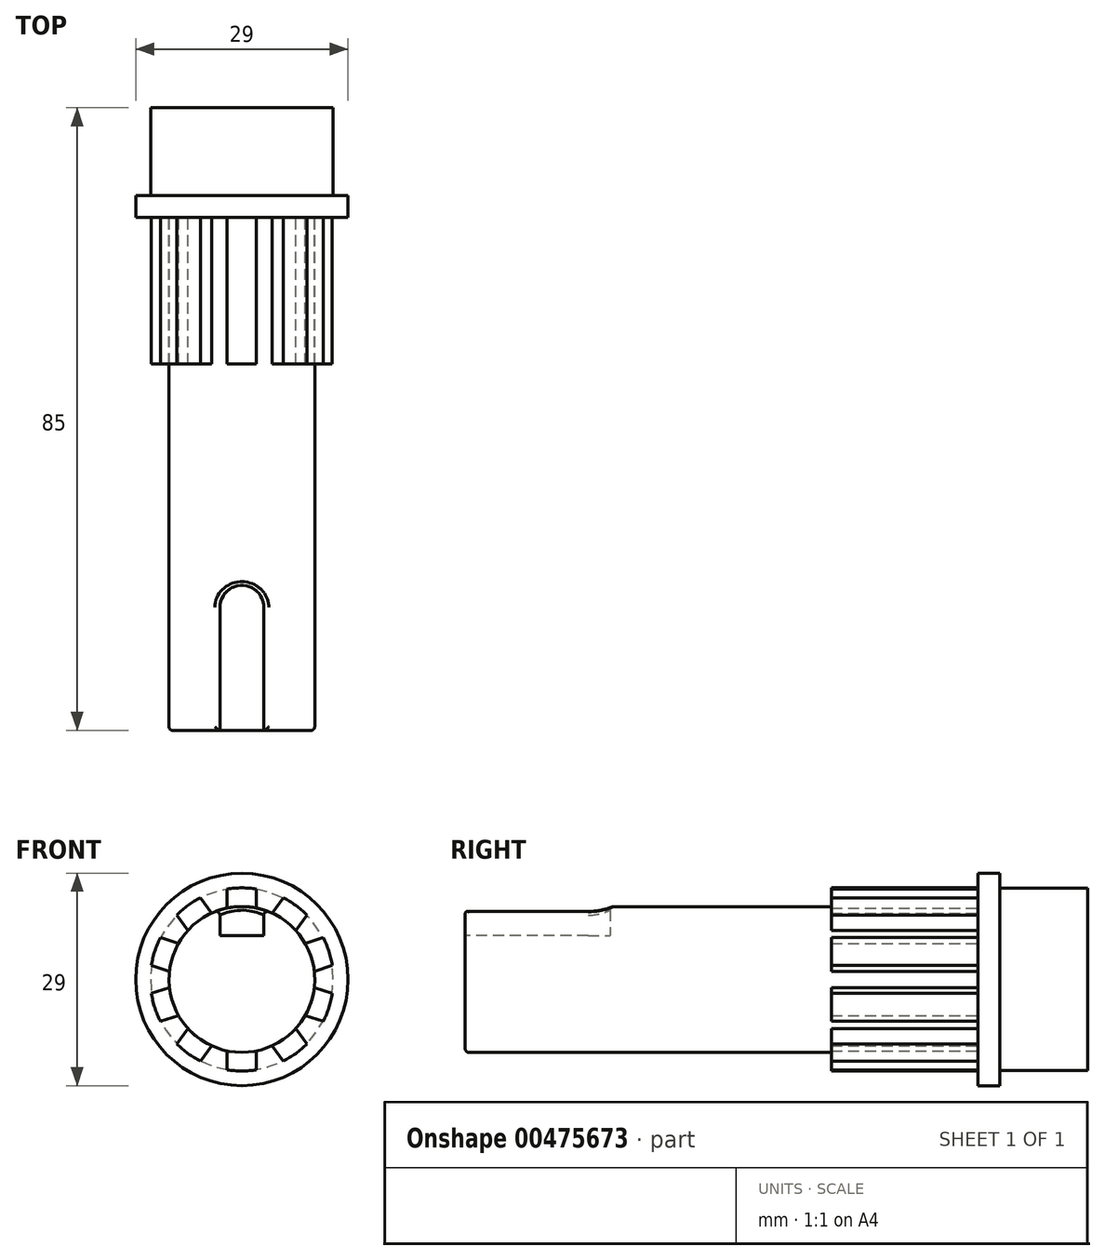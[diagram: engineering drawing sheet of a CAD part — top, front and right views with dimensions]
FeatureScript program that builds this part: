
annotation { "Feature Type Name" : "Feature", "Feature Type Description" : "" }
export const myFeature = defineFeature(function(context is Context, id is Id, definition is map)
    precondition{}
    {
        {
            var Q0;
            Q0=qCreatedBy(makeId("Front.planeOp"),FACE);
            var sketch = newSketch(context, id + "F0", { "sketchPlane" : qUnion([Q0])});
            skCircle(sketch, "E0", {"center": v(0, 0) * mm, "radius": 14.5 * mm});
            skCircle(sketch, "E1", {"center": v(0, 0) * mm, "radius": 12.45 * mm});
            skCircle(sketch, "E2", {"center": v(0, 0) * mm, "radius": 9.95 * mm});
            skSolve(sketch);
        }
        {
            var Q0;
            Q0=makeQuery(id+"F0.imprint","IMPRINT",FACE,{"disambiguationData":[TD([[makeQuery(id+"F0.imprint","IMPRINT",EDGE,{"derivedFrom":sQuery(id+"F0.wireOp",EDGE,"E2")}),1.0]])]});
            var Q1;
            Q1=sQuery(id+"F0.wireOp",EDGE,"E2");
            extrude(context, id + "F1", {"entities" : qUnion([Q0]), "surfaceEntities" : qUnion([Q1]), "depth" : 70 * mm});
        }
        {
            var Q0;
            Q0=makeQuery(id+"F0.imprint","IMPRINT",FACE,{"disambiguationData":[TD([[makeQuery(id+"F0.imprint","IMPRINT",EDGE,{"derivedFrom":sQuery(id+"F0.wireOp",EDGE,"E1")}),1.0]])]});
            var Q1;
            Q1=makeQuery(id+"F0.imprint","IMPRINT",FACE,{"disambiguationData":[TD([[makeQuery(id+"F0.imprint","IMPRINT",EDGE,{"derivedFrom":sQuery(id+"F0.wireOp",EDGE,"E2")}),1.0]])]});
            extrude(context, id + "F2", {"entities" : qUnion([Q0, Q1]), "operationType" : NewBodyOperationType.ADD, "oppositeDirection" : true, "depth" : 15 * mm});
        }
        {
            var Q0;
            Q0=makeQuery(id+"F0.imprint","IMPRINT",FACE,{"disambiguationData":[TD([[makeQuery(id+"F0.imprint","IMPRINT",EDGE,{"derivedFrom":sQuery(id+"F0.wireOp",EDGE,"E1")}),1.0]])]});
            var Q1;
            Q1=makeQuery(id+"F0.imprint","IMPRINT",FACE,{"disambiguationData":[TD([[makeQuery(id+"F0.imprint","IMPRINT",EDGE,{"derivedFrom":sQuery(id+"F0.wireOp",EDGE,"E2")}),1.0]])]});
            var Q2;
            Q2=makeQuery(id+"F0.imprint","IMPRINT",FACE,{"disambiguationData":[TD([[makeQuery(id+"F0.imprint","IMPRINT",EDGE,{"derivedFrom":sQuery(id+"F0.wireOp",EDGE,"E0")}),1.0]])]});
            extrude(context, id + "F3", {"entities" : qUnion([Q0, Q1, Q2]), "operationType" : NewBodyOperationType.ADD, "oppositeDirection" : true, "depth" : 3 * mm});
        }
        {
            var Q0;
            Q0=qCreatedBy(makeId("Front.planeOp"),FACE);
            var sketch = newSketch(context, id + "F4", { "sketchPlane" : qUnion([Q0])});
            skArc(sketch, "E3", {"start": v(2, 9.75) * mm, "mid": v(0, 9.95) * mm, "end": v(-2, 9.75) * mm});
            skArc(sketch, "E4", {"start": v(2, 12.34) * mm, "mid": v(0, 12.5) * mm, "end": v(-2, 12.34) * mm});
            skLineSegment(sketch, "E5.left", {"start": v(-2, 12.34) * mm, "end": v(-2, 9.75) * mm});
            skLineSegment(sketch, "E5.right", {"start": v(2, 12.34) * mm, "end": v(2, 9.75) * mm});
            skArc(sketch, "E6.trimOffspring", {"start": v(-2, -9.75) * mm, "mid": v(0, -9.95) * mm, "end": v(2, -9.75) * mm});
            skPoint(sketch, "E7.trimOffspring.start.orphan", {"position": v(-2, -12.34) * mm});
            skPoint(sketch, "E8.trimOffspring.end.orphan", {"position": v(2, -12.34) * mm});
            skLineSegment(sketch, "E9.1.0", {"start": v(-5.63, 11.16) * mm, "end": v(-4.11, 9.06) * mm});
            skArc(sketch, "E9.1.1", {"start": v(-5.63, 11.16) * mm, "mid": v(-7.35, 10.11) * mm, "end": v(-8.87, 8.8) * mm});
            skLineSegment(sketch, "E9.1.2", {"start": v(-8.87, 8.8) * mm, "end": v(-7.35, 6.7) * mm});
            skArc(sketch, "E9.1.3", {"start": v(-4.11, 9.06) * mm, "mid": v(-5.85, 8.05) * mm, "end": v(-7.35, 6.7) * mm});
            skLineSegment(sketch, "E9.2.0", {"start": v(-11.12, 5.72) * mm, "end": v(-8.65, 4.91) * mm});
            skArc(sketch, "E9.2.1", {"start": v(-11.12, 5.72) * mm, "mid": v(-11.89, 3.86) * mm, "end": v(-12.35, 1.91) * mm});
            skLineSegment(sketch, "E9.2.2", {"start": v(-12.35, 1.91) * mm, "end": v(-9.89, 1.1) * mm});
            skArc(sketch, "E9.2.3", {"start": v(-8.65, 4.91) * mm, "mid": v(-9.46, 3.07) * mm, "end": v(-9.89, 1.1) * mm});
            skLineSegment(sketch, "E9.3.0", {"start": v(-12.35, -1.91) * mm, "end": v(-9.89, -1.1) * mm});
            skArc(sketch, "E9.3.1", {"start": v(-12.35, -1.91) * mm, "mid": v(-11.89, -3.86) * mm, "end": v(-11.12, -5.72) * mm});
            skLineSegment(sketch, "E9.3.2", {"start": v(-11.12, -5.72) * mm, "end": v(-8.65, -4.91) * mm});
            skArc(sketch, "E9.3.3", {"start": v(-9.89, -1.1) * mm, "mid": v(-9.46, -3.07) * mm, "end": v(-8.65, -4.91) * mm});
            skLineSegment(sketch, "E9.4.0", {"start": v(-8.87, -8.8) * mm, "end": v(-7.35, -6.7) * mm});
            skArc(sketch, "E9.4.1", {"start": v(-8.87, -8.8) * mm, "mid": v(-7.35, -10.11) * mm, "end": v(-5.63, -11.16) * mm});
            skLineSegment(sketch, "E9.4.2", {"start": v(-5.63, -11.16) * mm, "end": v(-4.11, -9.06) * mm});
            skArc(sketch, "E9.4.3", {"start": v(-7.35, -6.7) * mm, "mid": v(-5.85, -8.05) * mm, "end": v(-4.11, -9.06) * mm});
            skLineSegment(sketch, "E9.5.0", {"start": v(-2, -12.34) * mm, "end": v(-2, -9.75) * mm});
            skArc(sketch, "E9.5.1", {"start": v(-2, -12.34) * mm, "mid": v(0, -12.5) * mm, "end": v(2, -12.34) * mm});
            skLineSegment(sketch, "E9.5.2", {"start": v(2, -12.34) * mm, "end": v(2, -9.75) * mm});
            skLineSegment(sketch, "E9.6.0", {"start": v(5.63, -11.16) * mm, "end": v(4.11, -9.06) * mm});
            skArc(sketch, "E9.6.1", {"start": v(5.63, -11.16) * mm, "mid": v(7.35, -10.11) * mm, "end": v(8.87, -8.8) * mm});
            skLineSegment(sketch, "E9.6.2", {"start": v(8.87, -8.8) * mm, "end": v(7.35, -6.7) * mm});
            skArc(sketch, "E9.6.3", {"start": v(4.11, -9.06) * mm, "mid": v(5.85, -8.05) * mm, "end": v(7.35, -6.7) * mm});
            skLineSegment(sketch, "E9.7.0", {"start": v(11.12, -5.72) * mm, "end": v(8.65, -4.91) * mm});
            skArc(sketch, "E9.7.1", {"start": v(11.12, -5.72) * mm, "mid": v(11.89, -3.86) * mm, "end": v(12.35, -1.91) * mm});
            skLineSegment(sketch, "E9.7.2", {"start": v(12.35, -1.91) * mm, "end": v(9.89, -1.1) * mm});
            skArc(sketch, "E9.7.3", {"start": v(8.65, -4.91) * mm, "mid": v(9.46, -3.07) * mm, "end": v(9.89, -1.1) * mm});
            skLineSegment(sketch, "E9.8.0", {"start": v(12.35, 1.91) * mm, "end": v(9.89, 1.1) * mm});
            skArc(sketch, "E9.8.1", {"start": v(12.35, 1.91) * mm, "mid": v(11.89, 3.86) * mm, "end": v(11.12, 5.72) * mm});
            skLineSegment(sketch, "E9.8.2", {"start": v(11.12, 5.72) * mm, "end": v(8.65, 4.91) * mm});
            skArc(sketch, "E9.8.3", {"start": v(9.89, 1.1) * mm, "mid": v(9.46, 3.07) * mm, "end": v(8.65, 4.91) * mm});
            skLineSegment(sketch, "E9.9.0", {"start": v(8.87, 8.8) * mm, "end": v(7.35, 6.7) * mm});
            skArc(sketch, "E9.9.1", {"start": v(8.87, 8.8) * mm, "mid": v(7.35, 10.11) * mm, "end": v(5.63, 11.16) * mm});
            skLineSegment(sketch, "E9.9.2", {"start": v(5.63, 11.16) * mm, "end": v(4.11, 9.06) * mm});
            skArc(sketch, "E9.9.3", {"start": v(7.35, 6.7) * mm, "mid": v(5.85, 8.05) * mm, "end": v(4.11, 9.06) * mm});
            skSolve(sketch);
        }
        {
            var Q0;
            Q0=makeQuery(id+"F4.imprint","IMPRINT",FACE,{"disambiguationData":[TD([[makeQuery(id+"F4.imprint","IMPRINT",EDGE,{"derivedFrom":sQuery(id+"F4.wireOp",EDGE,"E9.7.0")}),-1.0]])]});
            var Q1;
            Q1=makeQuery(id+"F4.imprint","IMPRINT",FACE,{"disambiguationData":[TD([[makeQuery(id+"F4.imprint","IMPRINT",EDGE,{"derivedFrom":sQuery(id+"F4.wireOp",EDGE,"E9.6.0")}),-1.0]])]});
            var Q2;
            Q2=makeQuery(id+"F4.imprint","IMPRINT",FACE,{"disambiguationData":[TD([[makeQuery(id+"F4.imprint","IMPRINT",EDGE,{"derivedFrom":sQuery(id+"F4.wireOp",EDGE,"E9.5.0")}),-1.0]])]});
            var Q3;
            Q3=makeQuery(id+"F4.imprint","IMPRINT",FACE,{"disambiguationData":[TD([[makeQuery(id+"F4.imprint","IMPRINT",EDGE,{"derivedFrom":sQuery(id+"F4.wireOp",EDGE,"E9.4.0")}),-1.0]])]});
            var Q4;
            Q4=makeQuery(id+"F4.imprint","IMPRINT",FACE,{"disambiguationData":[TD([[makeQuery(id+"F4.imprint","IMPRINT",EDGE,{"derivedFrom":sQuery(id+"F4.wireOp",EDGE,"E9.3.0")}),-1.0]])]});
            var Q5;
            Q5=makeQuery(id+"F4.imprint","IMPRINT",FACE,{"disambiguationData":[TD([[makeQuery(id+"F4.imprint","IMPRINT",EDGE,{"derivedFrom":sQuery(id+"F4.wireOp",EDGE,"E9.2.0")}),-1.0]])]});
            var Q6;
            Q6=makeQuery(id+"F4.imprint","IMPRINT",FACE,{"disambiguationData":[TD([[makeQuery(id+"F4.imprint","IMPRINT",EDGE,{"derivedFrom":sQuery(id+"F4.wireOp",EDGE,"E9.1.0")}),-1.0]])]});
            var Q7;
            Q7=makeQuery(id+"F4.imprint","IMPRINT",FACE,{"disambiguationData":[TD([[makeQuery(id+"F4.imprint","IMPRINT",EDGE,{"derivedFrom":sQuery(id+"F4.wireOp",EDGE,"E3")}),-1.0]])]});
            var Q8;
            Q8=makeQuery(id+"F4.imprint","IMPRINT",FACE,{"disambiguationData":[TD([[makeQuery(id+"F4.imprint","IMPRINT",EDGE,{"derivedFrom":sQuery(id+"F4.wireOp",EDGE,"E9.9.0")}),-1.0]])]});
            var Q9;
            Q9=makeQuery(id+"F4.imprint","IMPRINT",FACE,{"disambiguationData":[TD([[makeQuery(id+"F4.imprint","IMPRINT",EDGE,{"derivedFrom":sQuery(id+"F4.wireOp",EDGE,"E9.8.0")}),-1.0]])]});
            extrude(context, id + "F5", {"entities" : qUnion([Q0, Q1, Q2, Q3, Q4, Q5, Q6, Q7, Q8, Q9]), "operationType" : NewBodyOperationType.ADD, "depth" : 20 * mm});
        }
        {
            var Q0;
            Q0=qCreatedBy(makeId("Top.planeOp"),FACE);
            cPlane(context, id + "F6", {"entities" : qUnion([Q0]), "cplaneType" : CPlaneType.OFFSET, "offset" : 6 * mm, "width" : 150 * mm, "height" : 150 * mm});
        }
        {
            var Q0;
            Q0=qCreatedBy(id+"F6.planeOp",FACE);
            var sketch = newSketch(context, id + "F7", { "sketchPlane" : qUnion([Q0])});
            skLineSegment(sketch, "E10.top", {"start": v(0, -73.2) * mm, "end": v(-3, -73.2) * mm});
            skLineSegment(sketch, "E10.right", {"start": v(-3, -53.2) * mm, "end": v(-3, -73.2) * mm});
            skLineSegment(sketch, "E11.top", {"start": v(0, -73.2) * mm, "end": v(3, -73.2) * mm});
            skLineSegment(sketch, "E11.right", {"start": v(3, -53.2) * mm, "end": v(3, -73.2) * mm});
            skArc(sketch, "E12", {"start": v(3, -53.2) * mm, "mid": v(0, -50.2) * mm, "end": v(-3, -53.2) * mm});
            skSolve(sketch);
        }
        {
            var Q0;
            Q0 = qSketchRegion(id + "F7", true);
            extrude(context, id + "F8", {"entities" : qUnion([Q0]), "operationType" : NewBodyOperationType.REMOVE, "depth" : 3.95 * mm});
        }
        {
            var Q0;
            Q0=makeQuery(id+"F1.opExtrude","CAP_EDGE",EDGE,{"disambiguationData":[OSD([sQuery(id+"F0.wireOp",EDGE,"E2")])],"isStart":false});
            var Q1;
            Q1=makeQuery(id+"F8.boolean.opBoolean","INTERSECT",EDGE,{"derivedFrom":[makeQuery(id+"F1.opExtrude","SWEPT_FACE",FACE,{"disambiguationData":[OSD([sQuery(id+"F0.wireOp",EDGE,"E2")])]}),makeQuery(id+"F8.opExtrude","SWEPT_FACE",FACE,{"disambiguationData":[OSD([sQuery(id+"F7.wireOp",EDGE,"E10.right")])]})]});
            var Q2;
            Q2=makeQuery(id+"F8.boolean.opBoolean","INTERSECT",EDGE,{"derivedFrom":[makeQuery(id+"F1.opExtrude","SWEPT_FACE",FACE,{"disambiguationData":[OSD([sQuery(id+"F0.wireOp",EDGE,"E2")])]}),makeQuery(id+"F8.opExtrude","SWEPT_FACE",FACE,{"disambiguationData":[OSD([sQuery(id+"F7.wireOp",EDGE,"E12")])]})]});
            var Q3;
            Q3=makeQuery(id+"F8.boolean.opBoolean","INTERSECT",EDGE,{"derivedFrom":[makeQuery(id+"F1.opExtrude","SWEPT_FACE",FACE,{"disambiguationData":[OSD([sQuery(id+"F0.wireOp",EDGE,"E2")])]}),makeQuery(id+"F8.opExtrude","SWEPT_FACE",FACE,{"disambiguationData":[OSD([sQuery(id+"F7.wireOp",EDGE,"E11.right")])]})]});
            fillet(context, id + "F9", {"entities" : qUnion([Q0, Q1, Q2, Q3]), "radius" : 0.5 * mm, "tangentPropagation" : true, "allowEdgeOverflow" : false});
        }
    });
